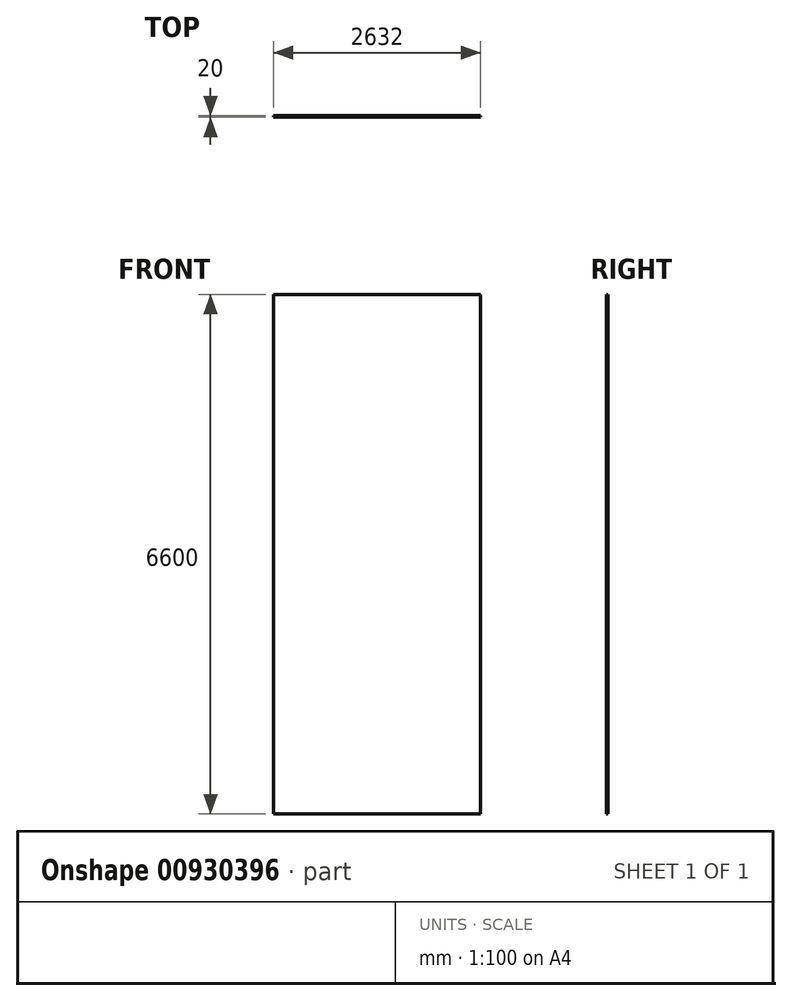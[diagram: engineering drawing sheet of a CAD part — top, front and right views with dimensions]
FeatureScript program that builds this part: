
annotation { "Feature Type Name" : "Feature", "Feature Type Description" : "" }
export const myFeature = defineFeature(function(context is Context, id is Id, definition is map)
    precondition{}
    {
        {
            var Q0;
            Q0=qCreatedBy(makeId("Front.planeOp"),FACE);
            var sketch = newSketch(context, id + "F0", { "sketchPlane" : qUnion([Q0])});
            skLineSegment(sketch, "E0.bottom", {"start": v(0, 0) * mm, "end": v(2632, 0) * mm});
            skLineSegment(sketch, "E0.top", {"start": v(0, 6600) * mm, "end": v(2632, 6600) * mm});
            skLineSegment(sketch, "E0.left", {"start": v(0, 0) * mm, "end": v(0, 6600) * mm});
            skLineSegment(sketch, "E0.right", {"start": v(2632, 0) * mm, "end": v(2632, 6600) * mm});
            skSolve(sketch);
        }
        {
            var Q0;
            Q0 = qSketchRegion(id + "F0", true);
            extrude(context, id + "F1", {"entities" : qUnion([Q0]), "depth" : 20 * mm, "offsetDistance" : 25 * mm});
        }
    });
